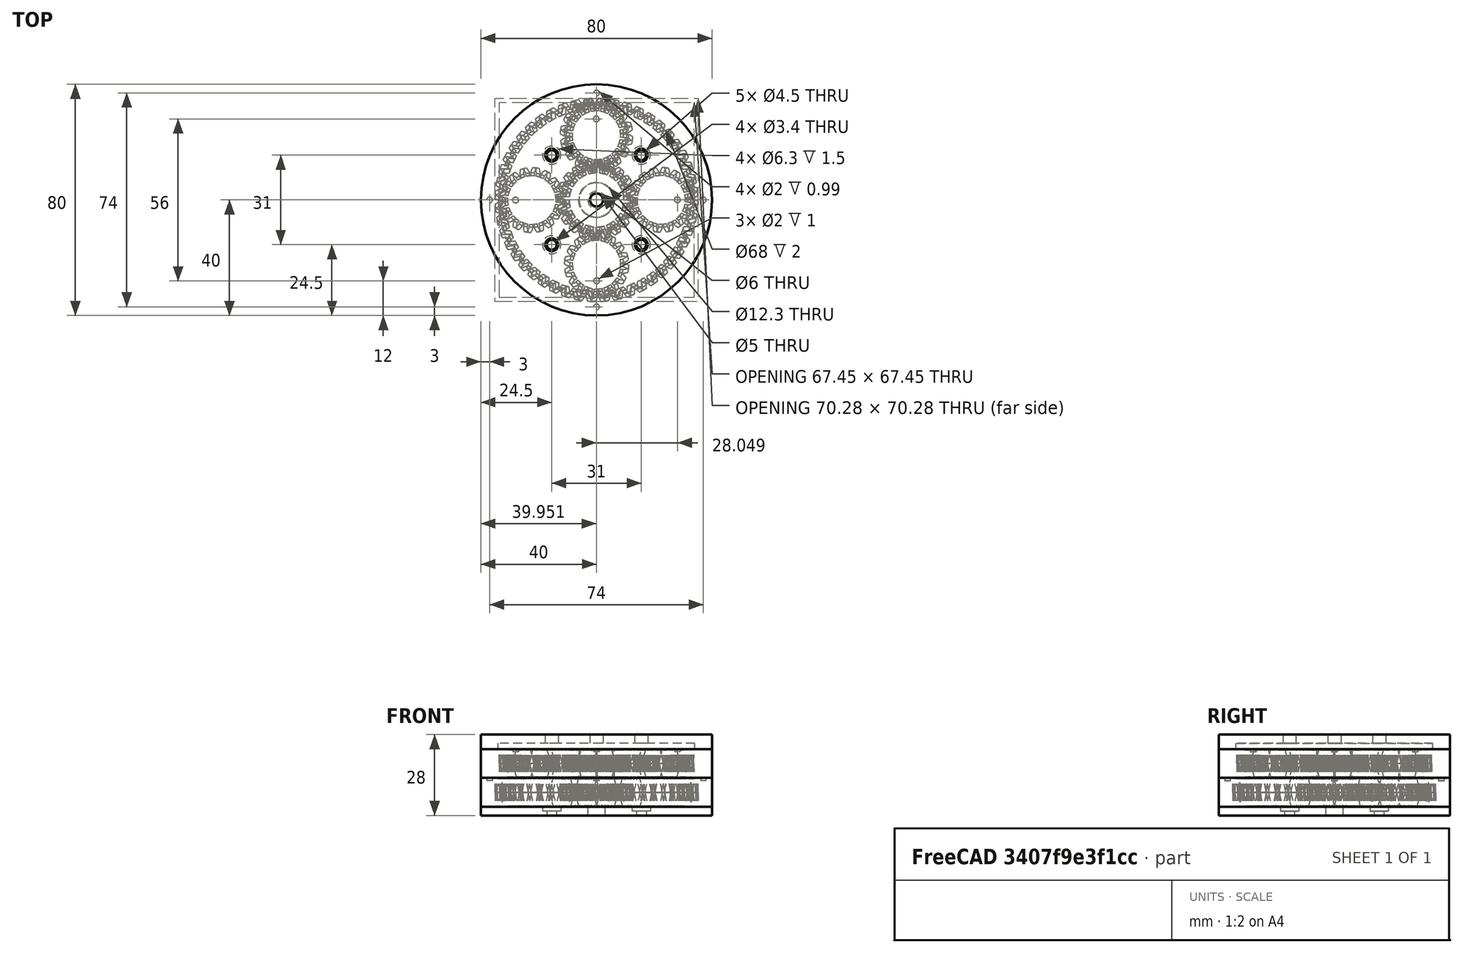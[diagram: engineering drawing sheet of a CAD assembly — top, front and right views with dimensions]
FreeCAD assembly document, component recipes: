
FREECAD ASSEMBLY — COMPONENT RECIPES ("gearbox")

This assembly document has 8 components, labeled P0..P7 below (a component is one placed body or linked part). 2 of them carry a construction recipe — the FreeCAD feature program that regenerates the part from scratch, quoted from this document or its linked companion documents; the rest are supplied as boundary geometry only. No exploded tour is included for this assembly.
COMPONENT P0 — recipe-attached ("Bottom Cap001", modeled in this document).
Construction recipe (the document's own serialized feature program — sketch geometry with constraints, then the solid features built on it; lengths are millimeters unless a unit is written):

FEATURE [Sketcher::SketchObject] Sketch
  AttachmentOffset = pos=(0,0,3) rot=(0,0,1;0rad)
  FullyConstrained = true
  MapMode = 5
  Placement = pos=(0,0,3) rot=(0,0,1;0rad)
  Support = -> [XY_Plane]
  sketch-geometry (9):
    g0: LineSegment StartX=-15.5 StartY=15.5 StartZ=0 EndX=-15.5 EndY=-15.5 EndZ=0
    g1: LineSegment StartX=-15.5 StartY=-15.5 StartZ=0 EndX=15.5 EndY=-15.5 EndZ=0
    g2: LineSegment StartX=15.5 StartY=-15.5 StartZ=0 EndX=15.5 EndY=15.5 EndZ=0
    g3: LineSegment StartX=15.5 StartY=15.5 StartZ=0 EndX=-15.5 EndY=15.5 EndZ=0
    g4: GeomPoint X=1e-16 Y=0 Z=0
    g5: Circle CenterX=-15.5 CenterY=15.5 CenterZ=0 NormalX=0 NormalY=0 NormalZ=1 AngleXU=0 Radius=1.75
    g6: Circle CenterX=15.5 CenterY=15.5 CenterZ=0 NormalX=0 NormalY=0 NormalZ=1 AngleXU=0 Radius=1.75
    g7: Circle CenterX=-15.5 CenterY=-15.5 CenterZ=0 NormalX=0 NormalY=0 NormalZ=1 AngleXU=0 Radius=1.75
    g8: Circle CenterX=15.5 CenterY=-15.5 CenterZ=0 NormalX=0 NormalY=0 NormalZ=1 AngleXU=0 Radius=1.75
  constraints (20):
    c: Coincident(g0,g1)
    c: Coincident(g1,g2)
    c: Coincident(g2,g3)
    c: Coincident(g3,g0)
    c: Horizontal(g1)
    c: Horizontal(g3)
    c: Vertical(g0)
    c: Vertical(g2)
    c: Symmetric(g1,g0,g4)
    c: Coincident(g4,g-1)
    c: Equal(g2,g3)
    c: Distance(g3) = 31
    c: Coincident(g5,g0)
    c: Coincident(g6,g2)
    c: Coincident(g7,g0)
    c: Coincident(g8,g1)
    c: Equal(g5,g6)
    c: Equal(g6,g7)
    c: Equal(g7,g8)
    c: Diameter(g6) = 3.5
FEATURE [PartDesign::FeatureBase] BaseFeature
  BaseFeature = -> Cut002
FEATURE [PartDesign::Hole] Hole
  BaseFeature = -> BaseFeature
  CustomThreadClearance = 0
  Depth = 25
  DepthType = 0
  Diameter = 3.4
  DrillForDepth = false
  DrillPoint = 1
  DrillPointAngle = 118
  HoleCutCountersinkAngle = 90
  HoleCutCustomValues = false
  HoleCutDepth = 1.5
  HoleCutDiameter = 6.3
  HoleCutType = 1
  ModelThread = false
  Profile = -> Sketch
  Tapered = false
  TaperedAngle = 90
  ThreadClass = 0
  ThreadDepth = 25
  ThreadDepthType = 0
  ThreadDirection = 0
  ThreadFit = 0
  ThreadSize = 9
  ThreadType = 1
  Threaded = false
  UseCustomThreadClearance = false
FEATURE [PartDesign::Body] Body  label="Bottom Cap001"
  BaseFeature = -> Cut002
  Group = -> [BaseFeature,Sketch,Hole]
  Origin = -> Origin
  Placement = pos=(0,0,-3) rot=(0,0,1;0rad)
  Tip = -> Hole
COMPONENT P1 — recipe-attached ("Body001", modeled in this document).
Construction recipe (the document's own serialized feature program — sketch geometry with constraints, then the solid features built on it; lengths are millimeters unless a unit is written):

FEATURE [PartDesign::FeatureBase] BaseFeature001
  BaseFeature = -> Cylinder004
FEATURE [Sketcher::SketchObject] Sketch001
  AttachmentOffset = pos=(0,0,3) rot=(0,0,1;0rad)
  FullyConstrained = true
  MapMode = 5
  Placement = pos=(0,0,3) rot=(0,0,1;0rad)
  Support = -> [XY_Plane001]
  sketch-geometry (9):
    g0: LineSegment StartX=-15.5 StartY=15.5 StartZ=0 EndX=-15.5 EndY=-15.5 EndZ=0
    g1: LineSegment StartX=-15.5 StartY=-15.5 StartZ=0 EndX=15.5 EndY=-15.5 EndZ=0
    g2: LineSegment StartX=15.5 StartY=-15.5 StartZ=0 EndX=15.5 EndY=15.5 EndZ=0
    g3: LineSegment StartX=15.5 StartY=15.5 StartZ=0 EndX=-15.5 EndY=15.5 EndZ=0
    g4: GeomPoint X=1e-16 Y=0 Z=0
    g5: Circle CenterX=-15.5 CenterY=15.5 CenterZ=0 NormalX=0 NormalY=0 NormalZ=1 AngleXU=0 Radius=1.75
    g6: Circle CenterX=15.5 CenterY=15.5 CenterZ=0 NormalX=0 NormalY=0 NormalZ=1 AngleXU=0 Radius=1.75
    g7: Circle CenterX=-15.5 CenterY=-15.5 CenterZ=0 NormalX=0 NormalY=0 NormalZ=1 AngleXU=0 Radius=1.75
    g8: Circle CenterX=15.5 CenterY=-15.5 CenterZ=0 NormalX=0 NormalY=0 NormalZ=1 AngleXU=0 Radius=1.75
  constraints (20):
    c: Coincident(g0,g1)
    c: Coincident(g1,g2)
    c: Coincident(g2,g3)
    c: Coincident(g3,g0)
    c: Horizontal(g1)
    c: Horizontal(g3)
    c: Vertical(g0)
    c: Vertical(g2)
    c: Symmetric(g1,g0,g4)
    c: Coincident(g4,g-1)
    c: Equal(g2,g3)
    c: Distance(g3) = 31
    c: Coincident(g5,g0)
    c: Coincident(g6,g2)
    c: Coincident(g7,g0)
    c: Coincident(g8,g1)
    c: Equal(g5,g6)
    c: Equal(g6,g7)
    c: Equal(g7,g8)
    c: Diameter(g6) = 3.5
FEATURE [PartDesign::Hole] Hole001
  BaseFeature = -> BaseFeature001
  CustomThreadClearance = 0
  Depth = 25
  DepthType = 0
  Diameter = 4.5
  DrillForDepth = false
  DrillPoint = 0
  DrillPointAngle = 118
  HoleCutCountersinkAngle = 90
  HoleCutCustomValues = false
  HoleCutDepth = 0
  HoleCutDiameter = 6.1
  HoleCutType = 0
  ModelThread = false
  Profile = -> Sketch001
  Tapered = false
  TaperedAngle = 90
  ThreadClass = 0
  ThreadDepth = 25
  ThreadDepthType = 0
  ThreadDirection = 0
  ThreadFit = 0
  ThreadSize = 11
  ThreadType = 1
  Threaded = false
  UseCustomThreadClearance = false
FEATURE [Sketcher::SketchObject] Sketch002
  FullyConstrained = true
  MapMode = 5
  Placement = pos=(0,0,3) rot=(0,0,1;0rad)
  Support = -> [Hole001]
  sketch-geometry (1):
    g0: Circle CenterX=0 CenterY=0 CenterZ=0 NormalX=0 NormalY=0 NormalZ=1 AngleXU=0 Radius=2.5
  constraints (2):
    c: Coincident(g0,g-1)
    c: Diameter(g0) = 5
FEATURE [PartDesign::Hole] Hole002
  BaseFeature = -> Hole001
  CustomThreadClearance = 0
  Depth = 25
  DepthType = 0
  Diameter = 4.5
  DrillForDepth = false
  DrillPoint = 1
  DrillPointAngle = 118
  HoleCutCountersinkAngle = 90
  HoleCutCustomValues = false
  HoleCutDepth = 0
  HoleCutDiameter = 6.1
  HoleCutType = 0
  ModelThread = false
  Profile = -> Sketch002
  Tapered = false
  TaperedAngle = 90
  ThreadClass = 0
  ThreadDepth = 25
  ThreadDepthType = 0
  ThreadDirection = 0
  ThreadFit = 0
  ThreadSize = 11
  ThreadType = 1
  Threaded = false
  UseCustomThreadClearance = false
FEATURE [PartDesign::Body] Body001
  BaseFeature = -> Cylinder004
  Group = -> [BaseFeature001,Sketch001,Hole001,Sketch002,Hole002]
  Origin = -> Origin001
  Placement = pos=(0,0,22) rot=(0,0,1;0rad)
  Tip = -> Hole002
COMPONENT P2 — geometry summary ("S1-Planet001"; no construction recipe available for this part):
  bounding box: 25.2 x 25.2 x 10.0 mm
  tessellated surface: 4,924 triangles
  volume: 3779 mm^3 (60% of its bounding box)
  symmetry: 4-fold rotationally symmetric about the z axis; mirror-symmetric across its z mid-plane
COMPONENT P3 — geometry summary ("S1-Planet002"; no construction recipe available for this part):
  bounding box: 25.2 x 25.2 x 10.0 mm
  tessellated surface: 4,924 triangles
  volume: 3779 mm^3 (60% of its bounding box)
  symmetry: 4-fold rotationally symmetric about the z axis; mirror-symmetric across its z mid-plane
COMPONENT P4 — geometry summary ("S1-Planet003"; no construction recipe available for this part):
  bounding box: 25.2 x 25.2 x 10.0 mm
  tessellated surface: 4,924 triangles
  volume: 3779 mm^3 (60% of its bounding box)
  symmetry: 4-fold rotationally symmetric about the z axis; mirror-symmetric across its z mid-plane
COMPONENT P5 — geometry summary ("S2-Planet001"; no construction recipe available for this part):
  bounding box: 22.4 x 22.4 x 10.0 mm
  tessellated surface: 5,276 triangles
  volume: 2986 mm^3 (60% of its bounding box)
  symmetry: 4-fold rotationally symmetric about the z axis; mirror-symmetric across its z mid-plane
COMPONENT P6 — geometry summary ("S2-Planet002"; no construction recipe available for this part):
  bounding box: 22.4 x 22.4 x 10.0 mm
  tessellated surface: 5,276 triangles
  volume: 2986 mm^3 (60% of its bounding box)
  symmetry: 4-fold rotationally symmetric about the z axis; mirror-symmetric across its z mid-plane
COMPONENT P7 — geometry summary ("S2-Planet003"; no construction recipe available for this part):
  bounding box: 22.4 x 22.4 x 10.0 mm
  tessellated surface: 5,276 triangles
  volume: 2986 mm^3 (60% of its bounding box)
  symmetry: 4-fold rotationally symmetric about the z axis; mirror-symmetric across its z mid-plane
PROVENANCE & LICENSES
A FreeCAD (.FCStd) document from a public repository crawl; recipes are the document's own serialized feature recipes (and, for linked parts, companion documents' recipes).
License: as declared in the source repository (recorded in the dataset sidecar).
